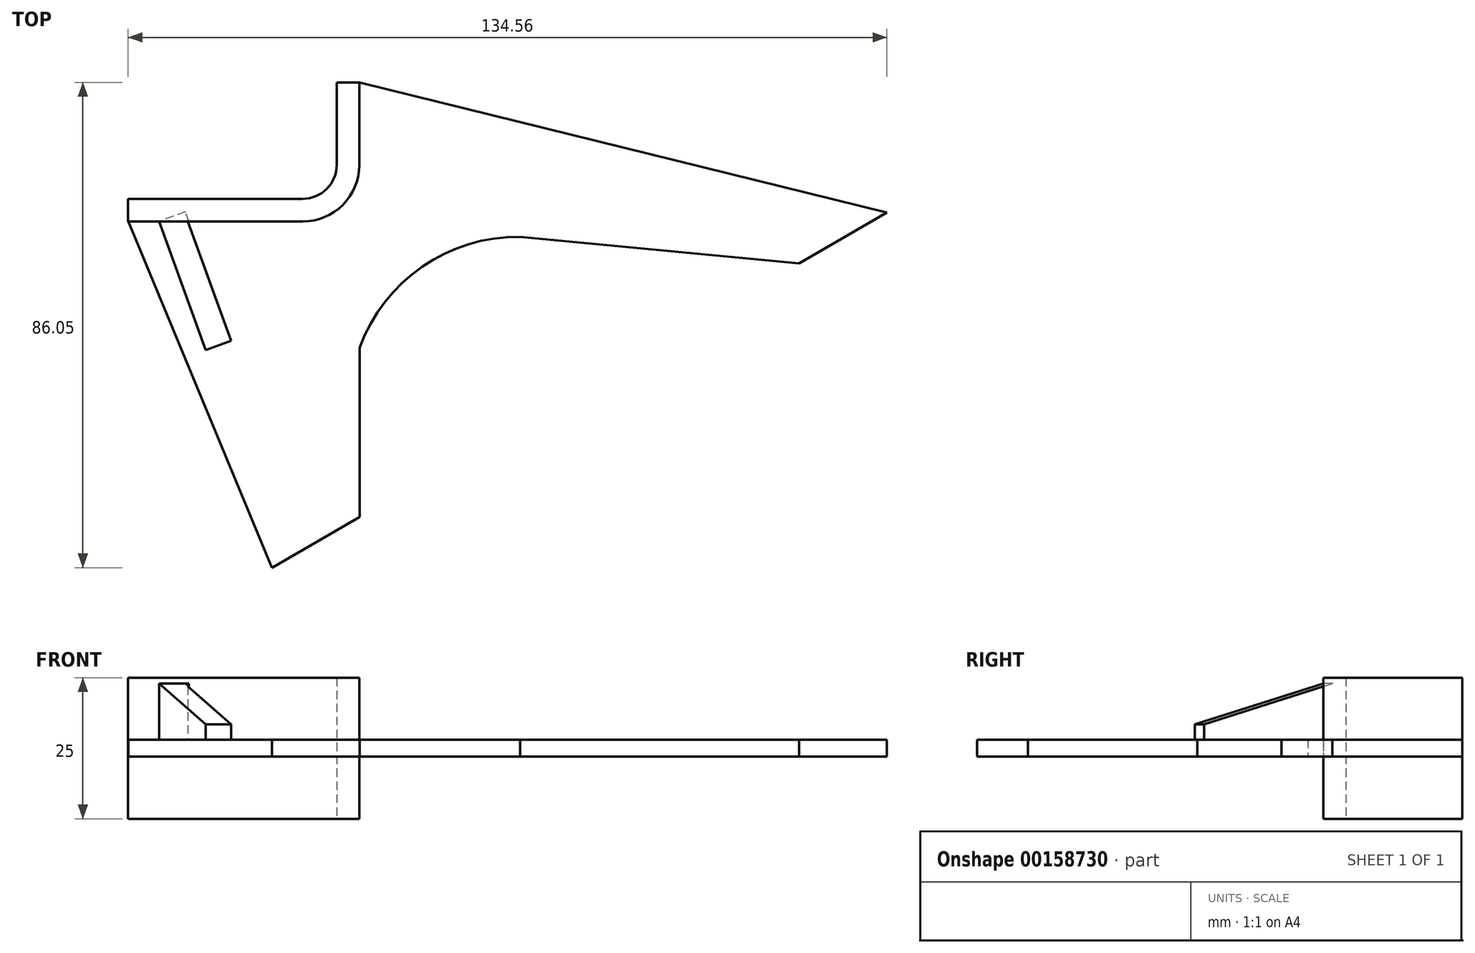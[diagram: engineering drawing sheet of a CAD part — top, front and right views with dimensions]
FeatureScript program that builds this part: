
annotation { "Feature Type Name" : "Feature", "Feature Type Description" : "" }
export const myFeature = defineFeature(function(context is Context, id is Id, definition is map)
    precondition{}
    {
        {
            var Q0;
            Q0=qCreatedBy(makeId("Top.planeOp"),FACE);
            var sketch = newSketch(context, id + "F0", { "sketchPlane" : qUnion([Q0])});
            skLineSegment(sketch, "E0", {"start": v(0, 24.64) * mm, "end": v(0, 10) * mm});
            skLineSegment(sketch, "E1", {"start": v(-41, 0) * mm, "end": v(-10, 0) * mm});
            skPoint(sketch, "E2.visualSharp", {"position": v(0, 0) * mm});
            skArc(sketch, "E2.filletArc", {"start": v(-10, 0) * mm, "mid": v(-2.93, 2.93) * mm, "end": v(0, 10) * mm});
            skLineSegment(sketch, "E3.0", {"start": v(-4, 24.64) * mm, "end": v(-4, 10) * mm});
            skArc(sketch, "E3.1", {"start": v(-10, 4) * mm, "mid": v(-5.76, 5.76) * mm, "end": v(-4, 10) * mm});
            skLineSegment(sketch, "E3.2", {"start": v(-41, 4) * mm, "end": v(-10, 4) * mm});
            skLineSegment(sketch, "E4", {"start": v(-4, 24.64) * mm, "end": v(-4, 24.64) * mm});
            skPoint(sketch, "E5.end.orphan", {"position": v(0, 30.23) * mm});
            skPoint(sketch, "E6.orphan", {"position": v(-2.7, 27.44) * mm});
            skPoint(sketch, "E7.start.orphan", {"position": v(0, 27.44) * mm});
            skLineSegment(sketch, "E8", {"start": v(0, 24.64) * mm, "end": v(-4, 24.64) * mm});
            skLineSegment(sketch, "E9", {"start": v(-41, 4) * mm, "end": v(-41, 0) * mm});
            skLineSegment(sketch, "E10", {"start": v(0, 0) * mm, "end": v(-66, 0) * mm});
            skLineSegment(sketch, "E11", {"start": v(-66, 0) * mm, "end": v(-66, -100) * mm});
            skLineSegment(sketch, "E12", {"start": v(-66, 0) * mm, "end": v(-66, 0) * mm});
            skLineSegment(sketch, "E13", {"start": v(0, 0) * mm, "end": v(-41, 0) * mm});
            skLineSegment(sketch, "E14", {"start": v(-25.5, 0) * mm, "end": v(-41, 0) * mm});
            skLineSegment(sketch, "E15.bottom", {"start": v(-25.29, -94.96) * mm, "end": v(121.94, -9.96) * mm});
            skLineSegment(sketch, "E15.top", {"start": v(-2.79, -133.93) * mm, "end": v(144.44, -48.93) * mm});
            skLineSegment(sketch, "E15.left", {"start": v(-25.29, -94.96) * mm, "end": v(-2.79, -133.93) * mm});
            skLineSegment(sketch, "E16", {"start": v(0, 24.64) * mm, "end": v(93.48, 1.57) * mm});
            skLineSegment(sketch, "E17", {"start": v(-41, 0) * mm, "end": v(-15.59, -61.4) * mm});
            skLineSegment(sketch, "E18", {"start": v(-15.59, -61.4) * mm, "end": v(0, -52.4) * mm});
            skLineSegment(sketch, "E19", {"start": v(0, -52.4) * mm, "end": v(0, -22.35) * mm});
            skLineSegment(sketch, "E20", {"start": v(93.48, 1.57) * mm, "end": v(77.9, -7.43) * mm});
            skLineSegment(sketch, "E21", {"start": v(77.9, -7.43) * mm, "end": v(28.44, -2.71) * mm});
            skArc(sketch, "E22", {"start": v(28.44, -2.71) * mm, "mid": v(11.1, -8.02) * mm, "end": v(0, -22.35) * mm});
            skSolve(sketch);
        }
        {
            var Q0;
            Q0 = qSketchRegion(id + "F0", true);
            extrude(context, id + "F1", {"entities" : qUnion([Q0]), "endBound" : BoundingType.SYMMETRIC, "depth" : 3 * mm});
        }
        {
            var Q0;
            Q0=qCreatedBy(makeId("Top.planeOp"),FACE);
            var sketch = newSketch(context, id + "F2", { "sketchPlane" : qUnion([Q0])});
            skLineSegment(sketch, "E23", {"start": v(-11.56, 1.58) * mm, "end": v(-0.9, -15.34) * mm});
            skLineSegment(sketch, "E24", {"start": v(-0.49, 8.27) * mm, "end": v(9.52, -9.05) * mm});
            skLineSegment(sketch, "E25", {"start": v(9.52, -9.05) * mm, "end": v(-0.9, -15.34) * mm});
            skLineSegment(sketch, "E26", {"start": v(-0.49, 8.27) * mm, "end": v(-11.56, 1.58) * mm});
            skSolve(sketch);
        }
        {
            var Q0;
            Q0 = qSketchRegion(id + "F2", true);
            extrude(context, id + "F3", {"entities" : qUnion([Q0]), "operationType" : NewBodyOperationType.ADD, "endBound" : BoundingType.SYMMETRIC, "depth" : 3 * mm});
        }
        {
            var Q0;
            Q0=qCreatedBy(makeId("Top.planeOp"),FACE);
            var sketch = newSketch(context, id + "F4", { "sketchPlane" : qUnion([Q0])});
            skLineSegment(sketch, "E27", {"start": v(-0.08, 24.65) * mm, "end": v(-0.08, 10.01) * mm});
            skArc(sketch, "E28.filletArc", {"start": v(-10.08, 0.01) * mm, "mid": v(-3, 2.94) * mm, "end": v(-0.08, 10.01) * mm});
            skLineSegment(sketch, "E29.0", {"start": v(-4.08, 24.65) * mm, "end": v(-4.08, 10.01) * mm});
            skArc(sketch, "E29.1", {"start": v(-10.08, 4.01) * mm, "mid": v(-5.84, 5.77) * mm, "end": v(-4.08, 10.01) * mm});
            skLineSegment(sketch, "E29.2", {"start": v(-41.08, 4.01) * mm, "end": v(-10.08, 4.01) * mm});
            skLineSegment(sketch, "E30", {"start": v(-9.33, 43.65) * mm, "end": v(-9.33, 43.65) * mm});
            skLineSegment(sketch, "E31", {"start": v(-0.08, 24.65) * mm, "end": v(-4.08, 24.65) * mm});
            skLineSegment(sketch, "E32", {"start": v(-41.08, 4.01) * mm, "end": v(-41.08, 0.01) * mm});
            skLineSegment(sketch, "E33", {"start": v(-10.08, 0.01) * mm, "end": v(-41.08, 0.01) * mm});
            skSolve(sketch);
        }
        {
            var Q0;
            Q0 = qSketchRegion(id + "F4", true);
            extrude(context, id + "F5", {"entities" : qUnion([Q0]), "operationType" : NewBodyOperationType.ADD, "endBound" : BoundingType.SYMMETRIC, "depth" : 25 * mm});
        }
        {
            var Q0;
            Q0=makeQuery(id+"F1.opExtrude","CAP_FACE",FACE,{"disambiguationData":[OSD([sQuery(id+"F0.wireOp",EDGE,"E3.0"),sQuery(id+"F0.wireOp",EDGE,"E3.1"),sQuery(id+"F0.wireOp",EDGE,"E3.2"),sQuery(id+"F0.wireOp",EDGE,"E8"),sQuery(id+"F0.wireOp",EDGE,"E9"),sQuery(id+"F0.wireOp",EDGE,"E16"),sQuery(id+"F0.wireOp",EDGE,"E17"),sQuery(id+"F0.wireOp",EDGE,"E18"),sQuery(id+"F0.wireOp",EDGE,"E19"),sQuery(id+"F0.wireOp",EDGE,"E20"),sQuery(id+"F0.wireOp",EDGE,"E21"),sQuery(id+"F0.wireOp",EDGE,"E22")])],"isStart":false});
            var sketch = newSketch(context, id + "F6", { "sketchPlane" : qUnion([Q0])});
            skLineSegment(sketch, "E34.bottom", {"start": v(-27.29, -22.8) * mm, "end": v(-22.77, -21.15) * mm});
            skLineSegment(sketch, "E34.top", {"start": v(-35.8, 0.6) * mm, "end": v(-31.29, 2.24) * mm});
            skLineSegment(sketch, "E34.left", {"start": v(-27.29, -22.8) * mm, "end": v(-35.8, 0.6) * mm});
            skLineSegment(sketch, "E34.right", {"start": v(-22.77, -21.15) * mm, "end": v(-31.29, 2.24) * mm});
            skSolve(sketch);
        }
        {
            var Q0;
            Q0 = qSketchRegion(id + "F6", true);
            extrude(context, id + "F7", {"entities" : qUnion([Q0]), "operationType" : NewBodyOperationType.ADD, "depth" : 10 * mm});
        }
        {
            var Q0;
            Q0=makeQuery(id+"F7.opExtrude","SWEPT_FACE",FACE,{"disambiguationData":[OSD([sQuery(id+"F6.wireOp",EDGE,"E34.left")])]});
            var sketch = newSketch(context, id + "F8", { "sketchPlane" : qUnion([Q0])});
            skLineSegment(sketch, "E35", {"start": v(12.09, 4.22) * mm, "end": v(-12.18, 11.5) * mm});
            skLineSegment(sketch, "E36", {"start": v(-12.18, 11.5) * mm, "end": v(12.09, 11.5) * mm});
            skLineSegment(sketch, "E37", {"start": v(12.09, 11.5) * mm, "end": v(12.09, 4.22) * mm});
            skSolve(sketch);
        }
        {
            var Q0;
            Q0=makeQuery(id+"F8.imprint","IMPRINT",FACE,{"disambiguationData":[TD([[makeQuery(id+"F8.imprint","IMPRINT",EDGE,{"derivedFrom":sQuery(id+"F8.wireOp",EDGE,"E35")}),-1.0]])]});
            extrude(context, id + "F9", {"entities" : qUnion([Q0]), "operationType" : NewBodyOperationType.REMOVE, "oppositeDirection" : true, "depth" : 5 * mm});
        }
    });
